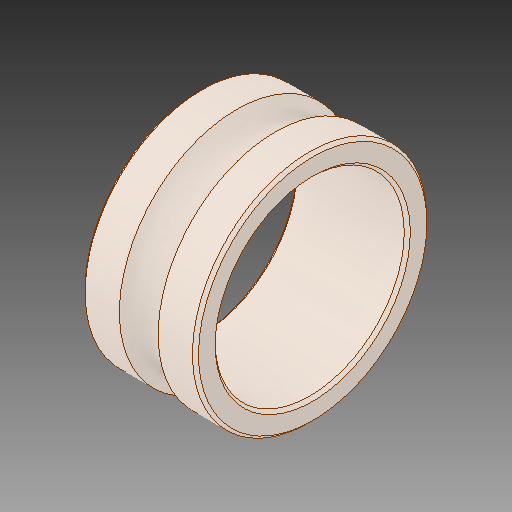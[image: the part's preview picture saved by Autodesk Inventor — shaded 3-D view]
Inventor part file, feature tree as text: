
AUTODESK INVENTOR PART (.ipt)
format: ipt  version: 2019 (Build 230136000, 136)  size: 157,184 bytes
history: mixed  units: mm
features: chamfer x1, imported_body x1
ambient origin geometry x8: Origin, YZ Plane, XZ Plane, XY Plane, X Axis, Y Axis, Z Axis, Center Point
bodies: Solid1 (imported_parasolid)
feature tree (2):
  chamfer  "Chamfer2"  [1 undecoded]
  imported_body  NMx_Import_Brep_tag  [imported B-rep: ~10 faces, bbox_mm=[3.0, 6.2, 0.0]]
note: 1 required parameter value undecoded (feature->parameter linkage not recoverable at this tier; creation-order binding heuristic only, values carry confidence <= 0.55)
